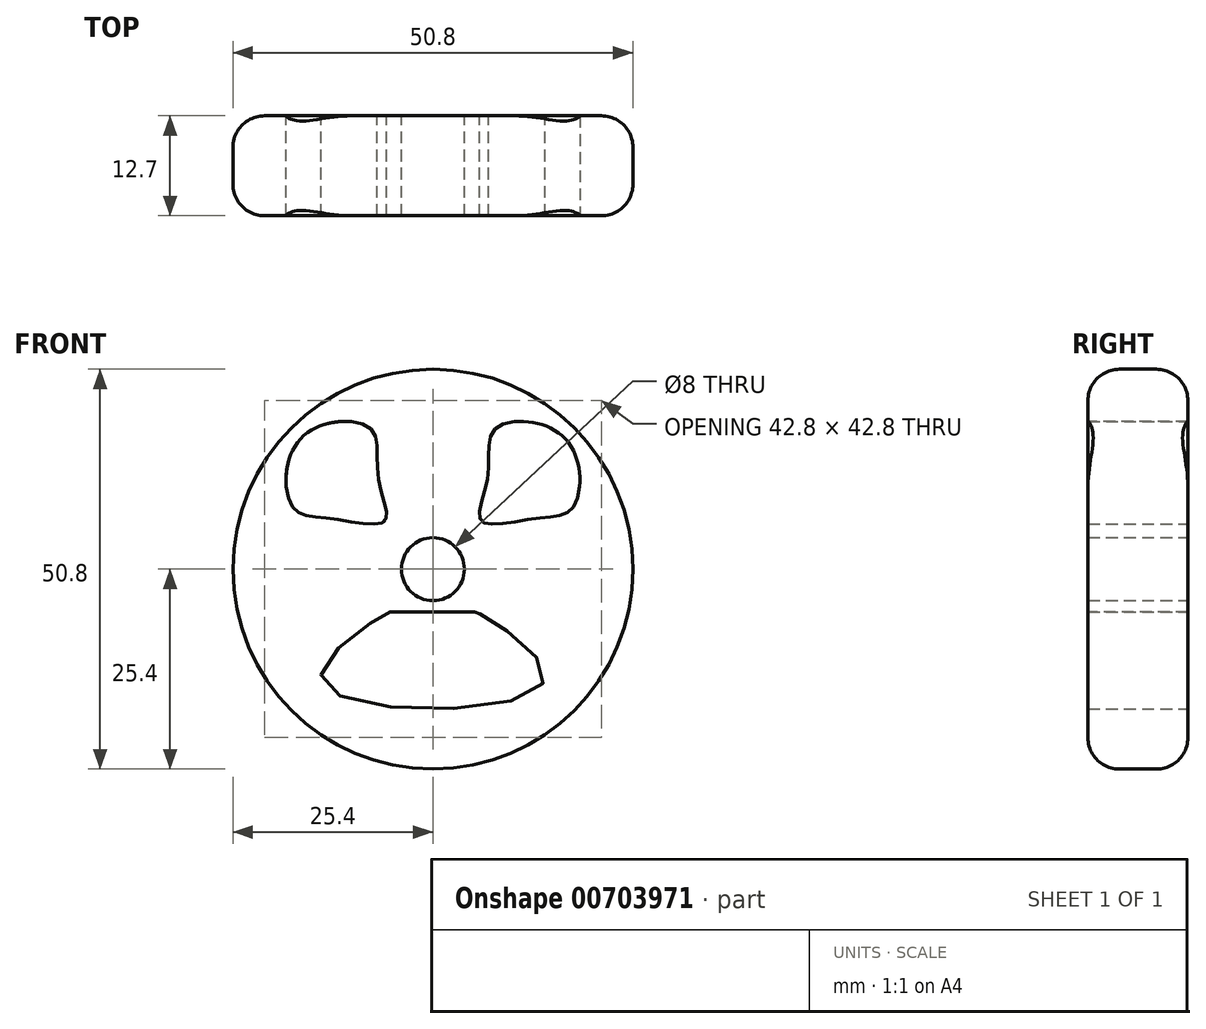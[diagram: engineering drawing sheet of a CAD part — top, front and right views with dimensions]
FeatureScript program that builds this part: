
annotation { "Feature Type Name" : "Feature", "Feature Type Description" : "" }
export const myFeature = defineFeature(function(context is Context, id is Id, definition is map)
    precondition{}
    {
        {
            var Q0;
            Q0=qCreatedBy(makeId("Front.planeOp"),FACE);
            var sketch = newSketch(context, id + "F0", { "sketchPlane" : qUnion([Q0])});
            skCircle(sketch, "E0", {"center": v(0, 0) * mm, "radius": 25.4 * mm});
            skCircle(sketch, "E1", {"center": v(0, 0) * mm, "radius": 4 * mm});
            skLineSegment(sketch, "E2", {"start": v(-17.96, 17.96) * mm, "end": v(0, 0) * mm, "construction": true});
            skLineSegment(sketch, "E3.MirrorCS", {"start": v(17.96, 17.96) * mm, "end": v(0, 0) * mm, "construction": true});
            skLineSegment(sketch, "E4", {"start": v(-14.15, -14.15) * mm, "end": v(14.15, -14.15) * mm, "construction": true});
            skLineSegment(sketch, "E5", {"start": v(-5.44, -5.44) * mm, "end": v(5.44, -5.44) * mm, "construction": true});
            skFitSpline(sketch, "E6", {"points": [v(-5.44, -5.44) * mm, v(-5.37, -5.44) * mm, v(-5.33, -5.44) * mm, v(-5.25, -5.44) * mm, v(-5.07, -5.44) * mm, v(-4.94, -5.44) * mm, v(-4.54, -5.44) * mm, v(-4.13, -5.44) * mm, v(-3.46, -5.44) * mm, v(-2.72, -5.44) * mm, v(0, -5.44) * mm, v(2.43, -5.44) * mm, v(3.14, -5.44) * mm, v(3.95, -5.44) * mm, v(4.25, -5.44) * mm, v(4.79, -5.44) * mm, v(4.98, -5.44) * mm, v(5.1, -5.44) * mm, v(5.2, -5.44) * mm, v(5.31, -5.44) * mm, v(5.36, -5.44) * mm, v(5.44, -5.44) * mm, v(14.15, -14.15) * mm, v(-14.15, -14.15) * mm, v(-5.44, -5.44) * mm]});
            skLineSegment(sketch, "E7", {"start": v(-12.92, 12.92) * mm, "end": v(-7.97, 17.87) * mm, "construction": true});
            skLineSegment(sketch, "E8.MirrorCS", {"start": v(-12.92, 12.92) * mm, "end": v(-17.87, 7.97) * mm, "construction": true});
            skFitSpline(sketch, "E9", {"points": [v(-17.87, 7.97) * mm, v(-16.7, 16.7) * mm, v(-7.97, 17.87) * mm, v(-6.98, 11.78) * mm, v(-6.13, 6.13) * mm, v(-13, 6.44) * mm, v(-17.87, 7.97) * mm]});
            skFitSpline(sketch, "E10.MirrorC", {"points": [v(17.87, 7.97) * mm, v(16.7, 16.7) * mm, v(7.97, 17.87) * mm, v(6.98, 11.78) * mm, v(6.13, 6.13) * mm, v(13, 6.44) * mm, v(17.87, 7.97) * mm]});
            skSolve(sketch);
        }
        {
            var Q0;
            Q0 = qSketchRegion(id + "F0", true);
            extrude(context, id + "F1", {"entities" : qUnion([Q0]), "depth" : 12.7 * mm, "offsetDistance" : 25 * mm});
        }
        {
            var Q0;
            Q0=makeQuery(id+"F1.opExtrude","CAP_EDGE",EDGE,{"disambiguationData":[OSD([sQuery(id+"F0.wireOp",EDGE,"E0")])],"isStart":true});
            var Q1;
            Q1=makeQuery(id+"F1.opExtrude","CAP_EDGE",EDGE,{"disambiguationData":[OSD([sQuery(id+"F0.wireOp",EDGE,"E0")])],"isStart":false});
            fillet(context, id + "F2", {"entities" : qUnion([Q0, Q1]), "radius" : 4 * mm, "tangentPropagation" : true, "allowEdgeOverflow" : false});
        }
    });
